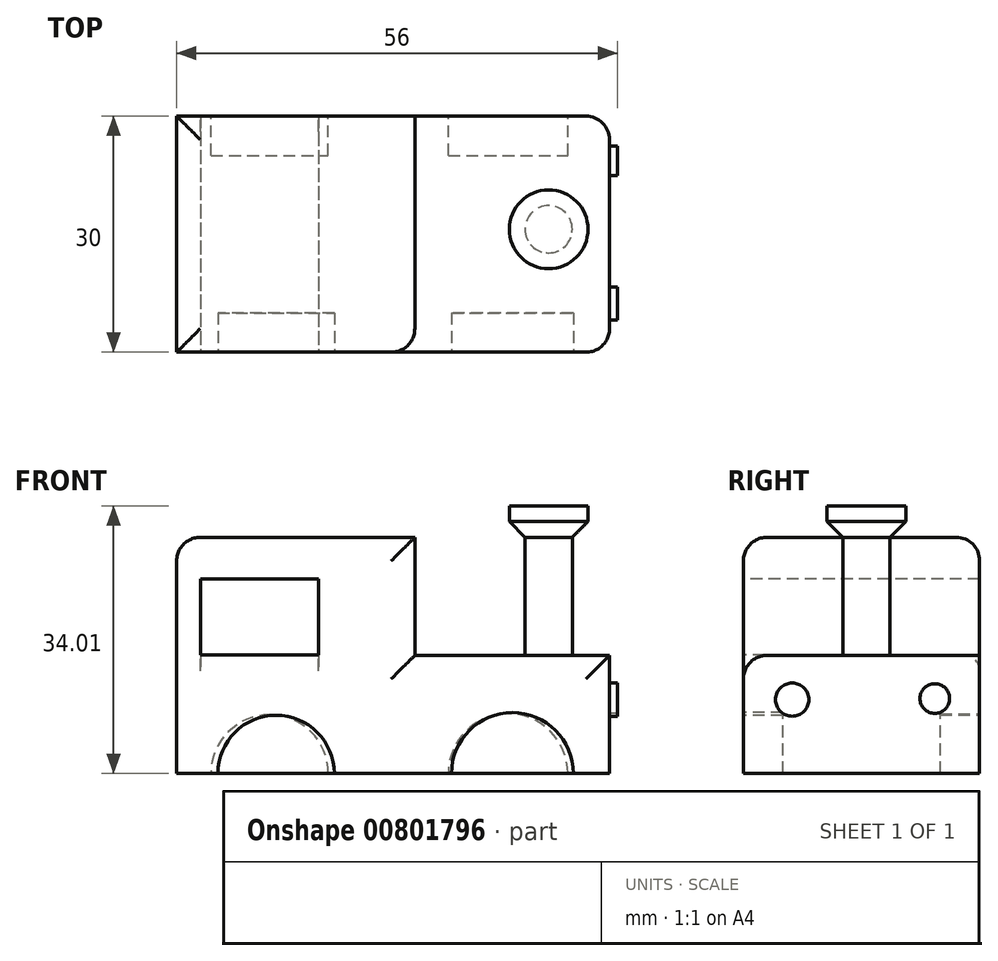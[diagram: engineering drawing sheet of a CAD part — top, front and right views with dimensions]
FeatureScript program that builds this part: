
annotation { "Feature Type Name" : "Feature", "Feature Type Description" : "" }
export const myFeature = defineFeature(function(context is Context, id is Id, definition is map)
    precondition{}
    {
        {
            var Q0;
            Q0=qCreatedBy(makeId("Top.planeOp"),FACE);
            var sketch = newSketch(context, id + "F0", { "sketchPlane" : qUnion([Q0])});
            skLineSegment(sketch, "E0.bottom", {"start": v(-21.74, -7.25) * mm, "end": v(33.26, -7.25) * mm});
            skLineSegment(sketch, "E0.top", {"start": v(-21.74, 22.75) * mm, "end": v(33.26, 22.75) * mm});
            skLineSegment(sketch, "E0.left", {"start": v(-21.74, -7.25) * mm, "end": v(-21.74, 22.75) * mm});
            skLineSegment(sketch, "E0.right", {"start": v(33.26, -7.25) * mm, "end": v(33.26, 22.75) * mm});
            skSolve(sketch);
        }
        {
            var Q0;
            Q0=makeQuery(id+"F0.imprint","IMPRINT",FACE,{"disambiguationData":[TD([[makeQuery(id+"F0.imprint","IMPRINT",EDGE,{"derivedFrom":sQuery(id+"F0.wireOp",EDGE,"E0.bottom")}),1.0]])]});
            extrude(context, id + "F1", {"entities" : qUnion([Q0]), "depth" : 30 * mm, "offsetDistance" : 25 * mm});
        }
        {
            var Q0;
            Q0=makeQuery(id+"F1.opExtrude","SWEPT_FACE",FACE,{"disambiguationData":[OSD([sQuery(id+"F0.wireOp",EDGE,"E0.top")])]});
            var sketch = newSketch(context, id + "F2", { "sketchPlane" : qUnion([Q0])});
            skLineSegment(sketch, "E1.bottom", {"start": v(-33.26, 30) * mm, "end": v(-8.52, 30) * mm});
            skLineSegment(sketch, "E1.top", {"start": v(-33.26, 15) * mm, "end": v(-8.52, 15) * mm});
            skLineSegment(sketch, "E1.left", {"start": v(-33.26, 30) * mm, "end": v(-33.26, 15) * mm});
            skLineSegment(sketch, "E1.right", {"start": v(-8.52, 30) * mm, "end": v(-8.52, 15) * mm});
            skSolve(sketch);
        }
        {
            var Q0;
            Q0=makeQuery(id+"F2.imprint","IMPRINT",FACE,{"disambiguationData":[TD([[makeQuery(id+"F2.imprint","IMPRINT",EDGE,{"derivedFrom":sQuery(id+"F2.wireOp",EDGE,"E1.bottom")}),1.0]])]});
            extrude(context, id + "F3", {"entities" : qUnion([Q0]), "operationType" : NewBodyOperationType.REMOVE, "oppositeDirection" : true, "depth" : 35 * mm, "offsetDistance" : 25 * mm});
        }
        {
            var Q0;
            Q0=makeQuery(id+"F1.opExtrude","SWEPT_FACE",FACE,{"disambiguationData":[OSD([sQuery(id+"F0.wireOp",EDGE,"E0.top")])]});
            var sketch = newSketch(context, id + "F4", { "sketchPlane" : qUnion([Q0])});
            skCircle(sketch, "E2", {"center": v(-20.36, 0) * mm, "radius": 7.6 * mm});
            skCircle(sketch, "E3", {"center": v(9.93, 0) * mm, "radius": 7.45 * mm});
            skSolve(sketch);
        }
        {
            var Q0;
            {var subQ0=sQuery(id+"F4.wireOp",EDGE,"E2");var subQ1=makeQuery(id+"F1.opExtrude","CAP_EDGE",EDGE,{"disambiguationData":[OSD([sQuery(id+"F0.wireOp",EDGE,"E0.top")])],"isStart":true});var subQ2=makeQuery(id+"F4.imprint","INTERSECT",VERTEX,{"disambiguationData":[OD(0.0)],"derivedFrom":[subQ1,subQ0]});Q0=makeQuery(id+"F4.imprint","IMPRINT",FACE,{"disambiguationData":[TD([[makeQuery(id+"F4.imprint","IMPRINT",EDGE,{"disambiguationData":[TD([[subQ2,1.0]])],"derivedFrom":subQ0}),1.0]])]});}
            var Q1;
            {var subQ0=sQuery(id+"F4.wireOp",EDGE,"E3");var subQ1=makeQuery(id+"F1.opExtrude","CAP_EDGE",EDGE,{"disambiguationData":[OSD([sQuery(id+"F0.wireOp",EDGE,"E0.top")])],"isStart":true});var subQ2=makeQuery(id+"F4.imprint","INTERSECT",VERTEX,{"disambiguationData":[OD(0.0)],"derivedFrom":[subQ1,subQ0]});Q1=makeQuery(id+"F4.imprint","IMPRINT",FACE,{"disambiguationData":[TD([[makeQuery(id+"F4.imprint","IMPRINT",EDGE,{"disambiguationData":[TD([[subQ2,-1.0]])],"derivedFrom":subQ0}),1.0]])]});}
            extrude(context, id + "F5", {"entities" : qUnion([Q0, Q1]), "operationType" : NewBodyOperationType.REMOVE, "oppositeDirection" : true, "depth" : 5 * mm, "offsetDistance" : 25 * mm});
        }
        {
            var Q0;
            Q0=makeQuery(id+"F1.opExtrude","SWEPT_FACE",FACE,{"disambiguationData":[OSD([sQuery(id+"F0.wireOp",EDGE,"E0.bottom")])]});
            var sketch = newSketch(context, id + "F6", { "sketchPlane" : qUnion([Q0])});
            skCircle(sketch, "E4", {"center": v(-9.1, 0) * mm, "radius": 7.4 * mm});
            skCircle(sketch, "E5", {"center": v(20.91, 0) * mm, "radius": 7.74 * mm});
            skSolve(sketch);
        }
        {
            var Q0;
            {var subQ0=sQuery(id+"F6.wireOp",EDGE,"E4");var subQ1=makeQuery(id+"F1.opExtrude","CAP_EDGE",EDGE,{"disambiguationData":[OSD([sQuery(id+"F0.wireOp",EDGE,"E0.bottom")])],"isStart":true});var subQ2=makeQuery(id+"F6.imprint","INTERSECT",VERTEX,{"disambiguationData":[OD(0.0)],"derivedFrom":[subQ1,subQ0]});Q0=makeQuery(id+"F6.imprint","IMPRINT",FACE,{"disambiguationData":[TD([[makeQuery(id+"F6.imprint","IMPRINT",EDGE,{"disambiguationData":[TD([[subQ2,1.0]])],"derivedFrom":subQ0}),1.0]])]});}
            var Q1;
            {var subQ0=sQuery(id+"F6.wireOp",EDGE,"E5");var subQ1=makeQuery(id+"F1.opExtrude","CAP_EDGE",EDGE,{"disambiguationData":[OSD([sQuery(id+"F0.wireOp",EDGE,"E0.bottom")])],"isStart":true});var subQ2=makeQuery(id+"F6.imprint","INTERSECT",VERTEX,{"disambiguationData":[OD(0.0)],"derivedFrom":[subQ1,subQ0]});Q1=makeQuery(id+"F6.imprint","IMPRINT",FACE,{"disambiguationData":[TD([[makeQuery(id+"F6.imprint","IMPRINT",EDGE,{"disambiguationData":[TD([[subQ2,-1.0]])],"derivedFrom":subQ0}),1.0]])]});}
            extrude(context, id + "F7", {"entities" : qUnion([Q0, Q1]), "operationType" : NewBodyOperationType.REMOVE, "oppositeDirection" : true, "depth" : 5 * mm, "offsetDistance" : 25 * mm});
        }
        {
            var Q0;
            Q0=makeQuery(id+"F3.boolean.opBoolean","INTERSECT",EDGE,{"derivedFrom":[makeQuery(id+"F1.opExtrude","SWEPT_FACE",FACE,{"disambiguationData":[OSD([sQuery(id+"F0.wireOp",EDGE,"E0.bottom")])]}),makeQuery(id+"F3.opExtrude","SWEPT_FACE",FACE,{"disambiguationData":[OSD([sQuery(id+"F2.wireOp",EDGE,"E1.right")])]})]});
            var Q1;
            Q1=makeQuery(id+"F3.boolean.opBoolean","COPY",EDGE,{"derivedFrom":makeQuery(id+"F3.opExtrude","CAP_EDGE",EDGE,{"disambiguationData":[OSD([sQuery(id+"F2.wireOp",EDGE,"E1.right")])],"isStart":true})});
            var Q2;
            Q2=makeQuery(id+"F1.opExtrude","SWEPT_EDGE",EDGE,{"disambiguationData":[OSD([sQuery(id+"F0.wireOp",EDGE,"E0.top"),sQuery(id+"F0.wireOp",EDGE,"E0.right")])]});
            var Q3;
            Q3=makeQuery(id+"F3.boolean.opBoolean","COPY",EDGE,{"derivedFrom":makeQuery(id+"F3.opExtrude","SWEPT_EDGE",EDGE,{"disambiguationData":[OSD([sQuery(id+"F0.wireOp",EDGE,"E0.top"),sQuery(id+"F0.wireOp",EDGE,"E0.right"),sQuery(id+"F2.wireOp",EDGE,"E1.top"),sQuery(id+"F2.wireOp",EDGE,"E1.left")])]})});
            var Q4;
            Q4=makeQuery(id+"F1.opExtrude","SWEPT_EDGE",EDGE,{"disambiguationData":[OSD([sQuery(id+"F0.wireOp",EDGE,"E0.bottom"),sQuery(id+"F0.wireOp",EDGE,"E0.right")])]});
            var Q5;
            Q5=makeQuery(id+"F3.boolean.opBoolean","COPY",EDGE,{"derivedFrom":makeQuery(id+"F3.opExtrude","SWEPT_EDGE",EDGE,{"disambiguationData":[OSD([sQuery(id+"F0.wireOp",EDGE,"E0.top"),sQuery(id+"F2.wireOp",EDGE,"E1.bottom"),sQuery(id+"F2.wireOp",EDGE,"E1.right")])]})});
            var Q6;
            Q6=makeQuery(id+"F1.opExtrude","CAP_EDGE",EDGE,{"disambiguationData":[OSD([sQuery(id+"F0.wireOp",EDGE,"E0.top")])],"isStart":false});
            var Q7;
            Q7=makeQuery(id+"F1.opExtrude","CAP_EDGE",EDGE,{"disambiguationData":[OSD([sQuery(id+"F0.wireOp",EDGE,"E0.left")])],"isStart":false});
            var Q8;
            Q8=makeQuery(id+"F3.boolean.opBoolean","COPY",EDGE,{"derivedFrom":makeQuery(id+"F3.opExtrude","CAP_EDGE",EDGE,{"disambiguationData":[OSD([sQuery(id+"F2.wireOp",EDGE,"E1.top")])],"isStart":true})});
            var Q9;
            Q9=makeQuery(id+"F3.boolean.opBoolean","INTERSECT",EDGE,{"derivedFrom":[makeQuery(id+"F1.opExtrude","SWEPT_FACE",FACE,{"disambiguationData":[OSD([sQuery(id+"F0.wireOp",EDGE,"E0.bottom")])]}),makeQuery(id+"F3.opExtrude","SWEPT_FACE",FACE,{"disambiguationData":[OSD([sQuery(id+"F2.wireOp",EDGE,"E1.top")])]})]});
            var Q10;
            Q10=makeQuery(id+"F1.opExtrude","CAP_EDGE",EDGE,{"disambiguationData":[OSD([sQuery(id+"F0.wireOp",EDGE,"E0.bottom")])],"isStart":false});
            fillet(context, id + "F8", {"entities" : qUnion([Q0, Q1, Q2, Q3, Q4, Q5, Q6, Q7, Q8, Q9, Q10]), "radius" : 3 * mm, "tangentPropagation" : true, "allowEdgeOverflow" : false});
        }
        {
            var Q0;
            Q0=makeQuery(id+"F1.opExtrude","SWEPT_FACE",FACE,{"disambiguationData":[OSD([sQuery(id+"F0.wireOp",EDGE,"E0.bottom")])]});
            var sketch = newSketch(context, id + "F9", { "sketchPlane" : qUnion([Q0])});
            skLineSegment(sketch, "E6.bottom", {"start": v(-18.7, 24.72) * mm, "end": v(-3.7, 24.72) * mm});
            skLineSegment(sketch, "E6.top", {"start": v(-18.7, 15.05) * mm, "end": v(-3.7, 15.05) * mm});
            skLineSegment(sketch, "E6.left", {"start": v(-18.7, 24.72) * mm, "end": v(-18.7, 15.05) * mm});
            skLineSegment(sketch, "E6.right", {"start": v(-3.7, 24.72) * mm, "end": v(-3.7, 15.05) * mm});
            skSolve(sketch);
        }
        {
            var Q0;
            Q0=makeQuery(id+"F9.imprint","IMPRINT",FACE,{"disambiguationData":[TD([[makeQuery(id+"F9.imprint","IMPRINT",EDGE,{"derivedFrom":sQuery(id+"F9.wireOp",EDGE,"E6.bottom")}),-1.0]])]});
            extrude(context, id + "F10", {"entities" : qUnion([Q0]), "operationType" : NewBodyOperationType.REMOVE, "oppositeDirection" : true, "depth" : 33.1 * mm, "offsetDistance" : 25 * mm});
        }
        {
            var Q0;
            Q0=makeQuery(id+"F10.boolean.opBoolean","INTERSECT",EDGE,{"derivedFrom":[makeQuery(id+"F1.opExtrude","SWEPT_FACE",FACE,{"disambiguationData":[OSD([sQuery(id+"F0.wireOp",EDGE,"E0.top")])]}),makeQuery(id+"F10.opExtrude","SWEPT_FACE",FACE,{"disambiguationData":[OSD([sQuery(id+"F9.wireOp",EDGE,"E6.top")])]})]});
            var Q1;
            Q1=makeQuery(id+"F10.boolean.opBoolean","COPY",EDGE,{"derivedFrom":makeQuery(id+"F10.opExtrude","CAP_EDGE",EDGE,{"disambiguationData":[OSD([sQuery(id+"F9.wireOp",EDGE,"E6.top")])],"isStart":true})});
            fillet(context, id + "F11", {"entities" : qUnion([Q0, Q1]), "radius" : 2 * mm, "tangentPropagation" : true, "allowEdgeOverflow" : false});
        }
        {
            var Q0;
            Q0=makeQuery(id+"F1.opExtrude","SWEPT_FACE",FACE,{"disambiguationData":[OSD([sQuery(id+"F0.wireOp",EDGE,"E0.right")])]});
            var sketch = newSketch(context, id + "F12", { "sketchPlane" : qUnion([Q0])});
            skCircle(sketch, "E7", {"center": v(-1.05, 9.38) * mm, "radius": 2.11 * mm});
            skCircle(sketch, "E8", {"center": v(17.06, 9.51) * mm, "radius": 1.88 * mm});
            skSolve(sketch);
        }
        {
            var Q0;
            Q0=makeQuery(id+"F12.imprint","IMPRINT",FACE,{"disambiguationData":[TD([[makeQuery(id+"F12.imprint","IMPRINT",EDGE,{"derivedFrom":sQuery(id+"F12.wireOp",EDGE,"E7")}),1.0]])]});
            var Q1;
            Q1=makeQuery(id+"F12.imprint","IMPRINT",FACE,{"disambiguationData":[TD([[makeQuery(id+"F12.imprint","IMPRINT",EDGE,{"derivedFrom":sQuery(id+"F12.wireOp",EDGE,"E8")}),1.0]])]});
            extrude(context, id + "F13", {"entities" : qUnion([Q0, Q1]), "operationType" : NewBodyOperationType.ADD, "depth" : 1 * mm, "offsetDistance" : 25 * mm});
        }
        {
            var Q0;
            Q0=makeQuery(id+"F3.boolean.opBoolean","COPY",FACE,{"derivedFrom":makeQuery(id+"F3.opExtrude","SWEPT_FACE",FACE,{"disambiguationData":[OSD([sQuery(id+"F2.wireOp",EDGE,"E1.top")])]})});
            var sketch = newSketch(context, id + "F14", { "sketchPlane" : qUnion([Q0])});
            skCircle(sketch, "E9", {"center": v(25.52, 8.37) * mm, "radius": 3 * mm});
            skSolve(sketch);
        }
        {
            var Q0;
            Q0=makeQuery(id+"F14.imprint","IMPRINT",FACE,{"disambiguationData":[TD([[makeQuery(id+"F14.imprint","IMPRINT",EDGE,{"derivedFrom":sQuery(id+"F14.wireOp",EDGE,"E9")}),1.0]])]});
            extrude(context, id + "F15", {"entities" : qUnion([Q0]), "operationType" : NewBodyOperationType.ADD, "depth" : 15 * mm, "offsetDistance" : 25 * mm});
        }
        {
            var Q0;
            Q0=makeQuery(id+"F15.opExtrude","CAP_FACE",FACE,{"disambiguationData":[OSD([sQuery(id+"F14.wireOp",EDGE,"E9")])],"isStart":false});
            var sketch = newSketch(context, id + "F16", { "sketchPlane" : qUnion([Q0])});
            skCircle(sketch, "E10", {"center": v(25.52, 8.37) * mm, "radius": 5 * mm});
            skSolve(sketch);
        }
        {
            var Q0;
            Q0 = qSketchRegion(id + "F16", true);
            extrude(context, id + "F17", {"entities" : qUnion([Q0]), "operationType" : NewBodyOperationType.ADD, "depth" : 4 * mm, "offsetDistance" : 25 * mm});
        }
        {
            var Q0;
            Q0=makeQuery(id+"F17.opExtrude","CAP_EDGE",EDGE,{"disambiguationData":[OSD([sQuery(id+"F16.wireOp",EDGE,"E10")])],"isStart":true});
            chamfer(context, id + "F18", {"entities" : qUnion([Q0]), "width" : 2 * mm, "tangentPropagation" : true});
        }
    });
